# Revit family: 306_bda720d7299641f29d68c2f2d41488
name_source: partatom
category: Pipe Accessories
units: mm (PartAtom-declared; Revit-internal decimal feet)

## family parameters
Always vertical = Yes
Cut with Voids When Loaded = No
Part Type = Valve - Breaks Into
Round Connector Dimension = Use Diameter
Shared = No
Work Plane-Based = No

## types (8) — shared parameters
CAT0 = Yes
Description = 3-way Control valve VLA131, PN16 internal thread
L2D_Min = 3048 mm
MC = No
Manufacturer = ESBE
QmdConnectorList = 301;D;302;D
URL = http://www.esbe.eu
Z4 = 13 mm
Z5 = 4 mm  [stored 0.0131234 ft]
Z6 = 2 mm  [stored 0.00656168 ft]
Z7 = 15 mm  [stored 0.0492126 ft]
magiPartTypeId = 306
magiProductFamilyId = bda720d7299641f29d68c2f2d41488

## per-type parameters (varying)
- VLA131 PN16 RP1 1/2 DN40-25: CenSd_D6_6=19 mm; CenSd_DN_6=33 mm; D=40 mm; D1=42 mm; D10=30 mm  [stored 0.0984252 ft]; D13=32 mm  [stored 0.104987 ft]; D2=34 mm; D3=30 mm  [stored 0.0984252 ft]; D4=27 mm; D5=29 mm; D6=22 mm; D7=15 mm  [stored 0.0492126 ft]; D8=8 mm  [stored 0.0262467 ft]; D9=7 mm  [stored 0.0229659 ft]; DN=38 mm; DN1=32 mm  [stored 0.104987 ft]; DN2=30 mm  [stored 0.0984252 ft]; H3=74 mm; H4=42 mm; L2=111 mm; L2D=150 mm; LT2=75 mm; W2D=40 mm; X1=5 mm  [stored 0.0164042 ft]; XN=15 mm  [stored 0.0492126 ft]; XN__ve=-15 mm  [stored -0.0492126 ft]; Z1=17 mm; Z11=11 mm; Z2=63 mm; Z8=9 mm  [stored 0.0295276 ft]; magiProductId=10c2d3b564284aa5a1ac0f65e7b3bf
- VLA131 PN16 RP3/4 DN20-6,3: CenSd_D6_6=12 mm  [stored 0.0393701 ft]; CenSd_DN_6=16 mm; D=20 mm; D1=28 mm; D10=15 mm  [stored 0.0492126 ft]; D13=21 mm  [stored 0.0688976 ft]; D2=22 mm; D3=20 mm  [stored 0.0656168 ft]; D4=18 mm; D5=19 mm; D6=14 mm  [stored 0.0459318 ft]; D7=10 mm  [stored 0.0328084 ft]; D8=5 mm  [stored 0.0164042 ft]; D9=5 mm  [stored 0.0164042 ft]; DN=19 mm; DN1=16 mm; DN2=15 mm  [stored 0.0492126 ft]; H3=61 mm; H4=30 mm  [stored 0.0984252 ft]; L2=74 mm; L2D=100 mm; LT2=50 mm; W2D=20 mm  [stored 0.0656168 ft]; X1=3 mm  [stored 0.00984252 ft]; XN=10 mm  [stored 0.0328084 ft]; XN__ve=-10 mm  [stored -0.0328084 ft]; Z1=15 mm  [stored 0.0492126 ft]; Z11=8 mm  [stored 0.0262467 ft]; Z2=45 mm; Z8=8 mm  [stored 0.0262467 ft]; magiProductId=5bd4c0f32cc84b52b8962c68906c69
- VLA131 PN16 RP2 DN50-38: CenSd_D6_6=22 mm; CenSd_DN_6=41 mm; D=50 mm; D1=50 mm; D10=38 mm; D13=38 mm; D2=40 mm; D3=36 mm; D4=33 mm; D5=34 mm; D6=26 mm; D7=18 mm; D8=9 mm  [stored 0.0295276 ft]; D9=8 mm  [stored 0.0262467 ft]; DN=48 mm; DN1=40 mm; DN2=38 mm; H3=90 mm; H4=53 mm; L2=133 mm; L2D=180 mm; LT2=90 mm; W2D=50 mm; X1=5 mm  [stored 0.0164042 ft]; XN=18 mm; XN__ve=-18 mm; Z1=21 mm  [stored 0.0688976 ft]; Z11=13 mm; Z2=80 mm; Z8=11 mm; magiProductId=2953d610b1b547d5bc6d682fdae015
- VLA131 PN16 RP1/2 DN15-4,0: CenSd_D6_6=11 mm; CenSd_DN_6=12 mm  [stored 0.0393701 ft]; D=15 mm; D1=24 mm; D10=11 mm; D13=18 mm; D2=19 mm; D3=17 mm; D4=15 mm  [stored 0.0492126 ft]; D5=16 mm; D6=12 mm  [stored 0.0393701 ft]; D7=9 mm  [stored 0.0295276 ft]; D8=4 mm  [stored 0.0131234 ft]; D9=4 mm  [stored 0.0131234 ft]; DN=14 mm  [stored 0.0459318 ft]; DN1=12 mm  [stored 0.0393701 ft]; DN2=11 mm; H3=58 mm; H4=24 mm; L2=63 mm; L2D=85 mm; LT2=43 mm; W2D=15 mm  [stored 0.0492126 ft]; X1=3 mm  [stored 0.00984252 ft]; XN=9 mm  [stored 0.0295276 ft]; XN__ve=-9 mm; Z1=16 mm; Z11=6 mm  [stored 0.019685 ft]; Z2=36 mm; Z8=8 mm  [stored 0.0262467 ft]; magiProductId=86cbdc7da5e8491681e885161fe1fe
- VLA131 PN16 RP1/2 DN15-2,5: CenSd_D6_6=11 mm; CenSd_DN_6=12 mm  [stored 0.0393701 ft]; D=15 mm; D1=24 mm; D10=11 mm; D13=18 mm; D2=19 mm; D3=17 mm; D4=15 mm  [stored 0.0492126 ft]; D5=16 mm; D6=12 mm  [stored 0.0393701 ft]; D7=9 mm  [stored 0.0295276 ft]; D8=4 mm  [stored 0.0131234 ft]; D9=4 mm  [stored 0.0131234 ft]; DN=14 mm  [stored 0.0459318 ft]; DN1=12 mm  [stored 0.0393701 ft]; DN2=11 mm; H3=58 mm; H4=24 mm; L2=63 mm; L2D=85 mm; LT2=43 mm; W2D=15 mm  [stored 0.0492126 ft]; X1=3 mm  [stored 0.00984252 ft]; XN=9 mm  [stored 0.0295276 ft]; XN__ve=-9 mm; Z1=16 mm; Z11=6 mm  [stored 0.019685 ft]; Z2=36 mm; Z8=8 mm  [stored 0.0262467 ft]; magiProductId=357b6429a2884e82b61f70fd2efe1c
- VLA131 PN16 RP1/2 DN15-1,6: CenSd_D6_6=11 mm; CenSd_DN_6=12 mm  [stored 0.0393701 ft]; D=15 mm; D1=24 mm; D10=11 mm; D13=18 mm; D2=19 mm; D3=17 mm; D4=15 mm  [stored 0.0492126 ft]; D5=16 mm; D6=12 mm  [stored 0.0393701 ft]; D7=9 mm  [stored 0.0295276 ft]; D8=4 mm  [stored 0.0131234 ft]; D9=4 mm  [stored 0.0131234 ft]; DN=14 mm  [stored 0.0459318 ft]; DN1=12 mm  [stored 0.0393701 ft]; DN2=11 mm; H3=58 mm; H4=24 mm; L2=63 mm; L2D=85 mm; LT2=43 mm; W2D=15 mm  [stored 0.0492126 ft]; X1=3 mm  [stored 0.00984252 ft]; XN=9 mm  [stored 0.0295276 ft]; XN__ve=-9 mm; Z1=16 mm; Z11=6 mm  [stored 0.019685 ft]; Z2=36 mm; Z8=8 mm  [stored 0.0262467 ft]; magiProductId=031b6205b3f64c0999590cb319f7af
- VLA131 PN16 RP1 DN25-10: CenSd_D6_6=14 mm  [stored 0.0459318 ft]; CenSd_DN_6=21 mm  [stored 0.0688976 ft]; D=25 mm; D1=32 mm  [stored 0.104987 ft]; D10=19 mm; D13=24 mm; D2=26 mm; D3=23 mm; D4=21 mm  [stored 0.0688976 ft]; D5=22 mm; D6=17 mm; D7=12 mm  [stored 0.0393701 ft]; D8=6 mm  [stored 0.019685 ft]; D9=5 mm  [stored 0.0164042 ft]; DN=24 mm; DN1=20 mm  [stored 0.0656168 ft]; DN2=19 mm; H3=65 mm; H4=34 mm; L2=85 mm; L2D=115 mm; LT2=58 mm; W2D=25 mm  [stored 0.082021 ft]; X1=3 mm  [stored 0.00984252 ft]; XN=12 mm  [stored 0.0393701 ft]; XN__ve=-12 mm; Z1=16 mm; Z11=9 mm  [stored 0.0295276 ft]; Z2=51 mm; Z8=8 mm  [stored 0.0262467 ft]; magiProductId=e242ae87362446a4a0f38f03c7b166
- VLA131 PN16 RP1 1/4 DN32-16: CenSd_D6_6=16 mm; CenSd_DN_6=26 mm; D=32 mm; D1=36 mm; D10=24 mm; D13=28 mm; D2=29 mm; D3=26 mm; D4=24 mm; D5=25 mm  [stored 0.082021 ft]; D6=19 mm; D7=13 mm; D8=7 mm  [stored 0.0229659 ft]; D9=6 mm  [stored 0.019685 ft]; DN=30 mm  [stored 0.0984252 ft]; DN1=26 mm; DN2=24 mm; H3=70 mm; H4=35 mm; L2=96 mm; L2D=130 mm; LT2=65 mm; W2D=32 mm  [stored 0.104987 ft]; X1=4 mm  [stored 0.0131234 ft]; XN=13 mm; XN__ve=-13 mm; Z1=18 mm; Z11=9 mm  [stored 0.0295276 ft]; Z2=53 mm; Z8=9 mm  [stored 0.0295276 ft]; magiProductId=04237824c23f4f919f73fc450508a4

note: column(s) folded — value = type name in every type: magiProductCode

note: [stored X ft] marks values corroborated as IEEE doubles in the binary element streams (Revit-internal decimal feet)

## geometry (parser evidence)
native form markers: Sweep x2
no freeform markers — native parametric forms only
